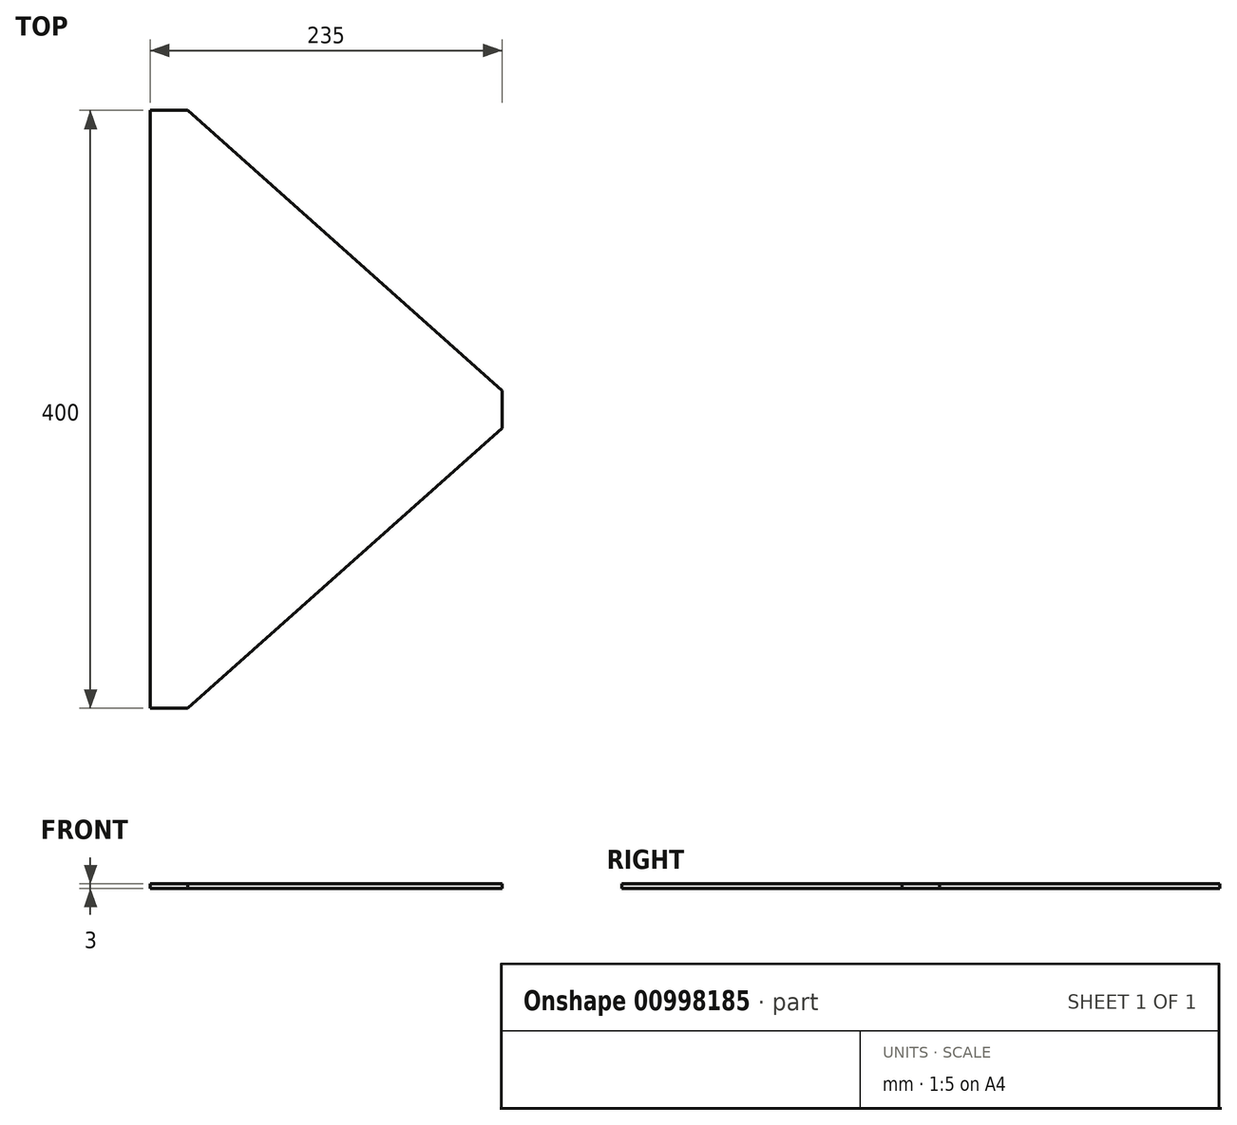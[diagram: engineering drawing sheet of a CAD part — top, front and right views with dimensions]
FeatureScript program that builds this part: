
annotation { "Feature Type Name" : "Feature", "Feature Type Description" : "" }
export const myFeature = defineFeature(function(context is Context, id is Id, definition is map)
    precondition{}
    {
        {
            var Q0;
            Q0=qCreatedBy(makeId("Top.planeOp"),FACE);
            var sketch = newSketch(context, id + "F0", { "sketchPlane" : qUnion([Q0])});
            skLineSegment(sketch, "E0.bottom", {"start": v(0, 0) * mm, "end": v(-1400, 0) * mm, "construction": true});
            skLineSegment(sketch, "E0.top", {"start": v(0, 800) * mm, "end": v(-1400, 800) * mm, "construction": true});
            skLineSegment(sketch, "E0.left", {"start": v(0, 0) * mm, "end": v(0, 800) * mm, "construction": true});
            skLineSegment(sketch, "E0.right", {"start": v(-1400, 0) * mm, "end": v(-1400, 800) * mm, "construction": true});
            skLineSegment(sketch, "E1", {"start": v(-700, 0) * mm, "end": v(-700, 800) * mm, "construction": true});
            skLineSegment(sketch, "E2", {"start": v(-700, 400) * mm, "end": v(0, 400) * mm, "construction": true});
            skLineSegment(sketch, "E3", {"start": v(0, 400) * mm, "end": v(-250, 400) * mm, "construction": true});
            skLineSegment(sketch, "E4", {"start": v(0, 800) * mm, "end": v(-460, 800) * mm, "construction": true});
            skLineSegment(sketch, "E5", {"start": v(-460, 800) * mm, "end": v(-460, 600) * mm, "construction": true});
            skLineSegment(sketch, "E6", {"start": v(-460, 600) * mm, "end": v(-485, 600) * mm});
            skLineSegment(sketch, "E7", {"start": v(-250, 400) * mm, "end": v(-250, 412.5) * mm});
            skLineSegment(sketch, "E8", {"start": v(-250, 412.5) * mm, "end": v(-460, 600) * mm});
            skLineSegment(sketch, "E9", {"start": v(-485, 600) * mm, "end": v(-485, 400) * mm});
            skLineSegment(sketch, "E10.MirrorCS", {"start": v(-485, 200) * mm, "end": v(-485, 400) * mm});
            skLineSegment(sketch, "E11.MirrorCS", {"start": v(-460, 200) * mm, "end": v(-485, 200) * mm});
            skLineSegment(sketch, "E12.MirrorCS", {"start": v(-250, 387.5) * mm, "end": v(-460, 200) * mm});
            skLineSegment(sketch, "E13.MirrorCS", {"start": v(-250, 400) * mm, "end": v(-250, 387.5) * mm});
            skSolve(sketch);
        }
        {
            var Q0;
            Q0 = qSketchRegion(id + "F0", true);
            extrude(context, id + "F1", {"entities" : qUnion([Q0]), "depth" : 3 * mm, "offsetDistance" : 25 * mm});
        }
    });
